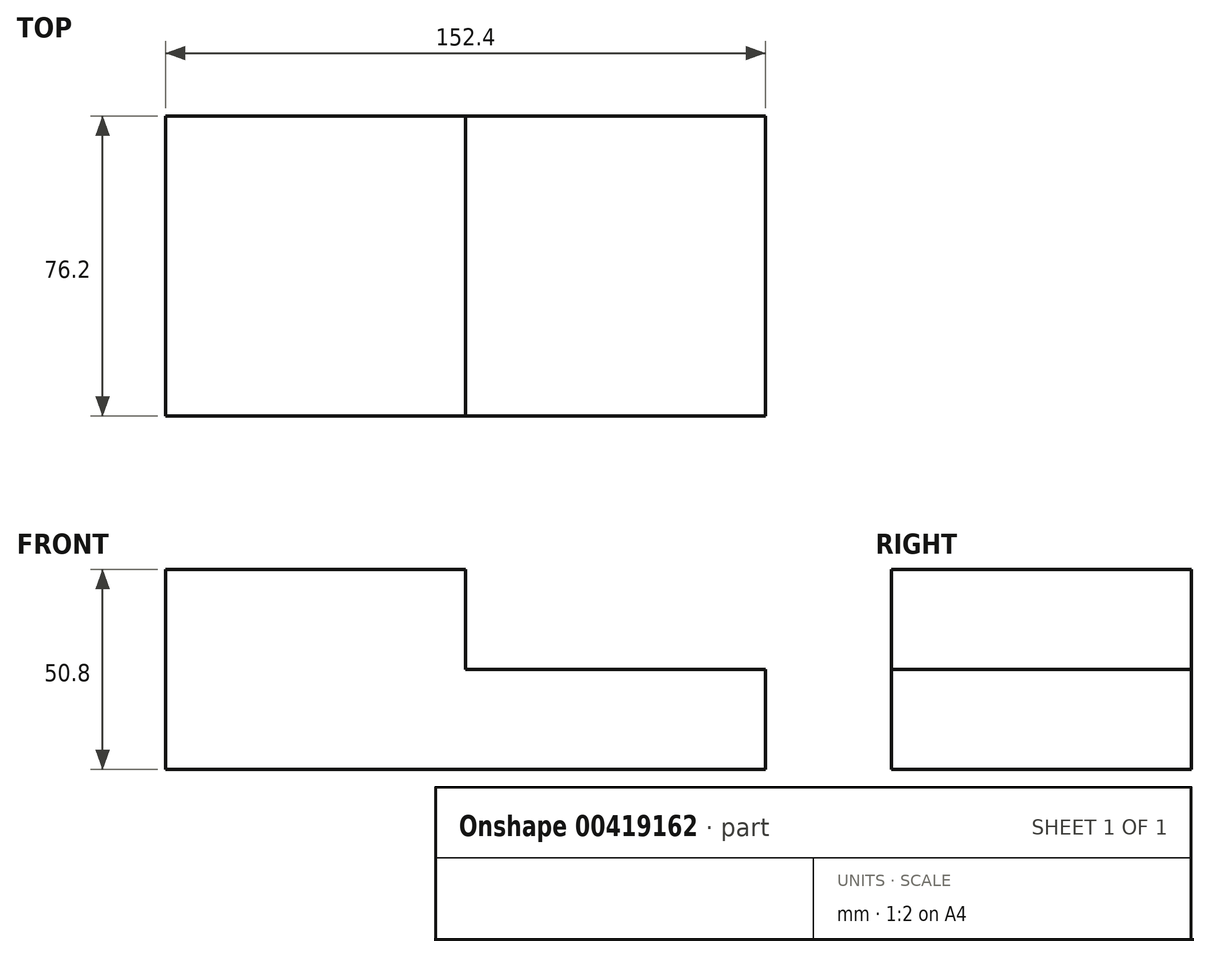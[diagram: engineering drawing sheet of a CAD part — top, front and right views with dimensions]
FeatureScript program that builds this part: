
annotation { "Feature Type Name" : "Feature", "Feature Type Description" : "" }
export const myFeature = defineFeature(function(context is Context, id is Id, definition is map)
    precondition{}
    {
        {
            var Q0;
            Q0=qCreatedBy(makeId("Front.planeOp"),FACE);
            var sketch = newSketch(context, id + "F0", { "sketchPlane" : qUnion([Q0])});
            skLineSegment(sketch, "E0", {"start": v(0, 0) * mm, "end": v(152.4, 0) * mm});
            skLineSegment(sketch, "E1", {"start": v(152.4, 0) * mm, "end": v(152.4, 25.4) * mm});
            skLineSegment(sketch, "E2", {"start": v(152.4, 25.4) * mm, "end": v(76.2, 25.4) * mm});
            skLineSegment(sketch, "E3", {"start": v(76.2, 25.4) * mm, "end": v(76.2, 50.8) * mm});
            skLineSegment(sketch, "E4", {"start": v(76.2, 50.8) * mm, "end": v(0, 50.8) * mm});
            skLineSegment(sketch, "E5", {"start": v(0, 50.8) * mm, "end": v(0, 0) * mm});
            skSolve(sketch);
        }
        {
            var Q0;
            Q0=makeQuery(id+"F0.imprint","IMPRINT",FACE,{"disambiguationData":[TD([[makeQuery(id+"F0.imprint","IMPRINT",EDGE,{"derivedFrom":sQuery(id+"F0.wireOp",EDGE,"E0")}),1.0]])]});
            extrude(context, id + "F1", {"entities" : qUnion([Q0]), "depth" : 76.2 * mm});
        }
    });
